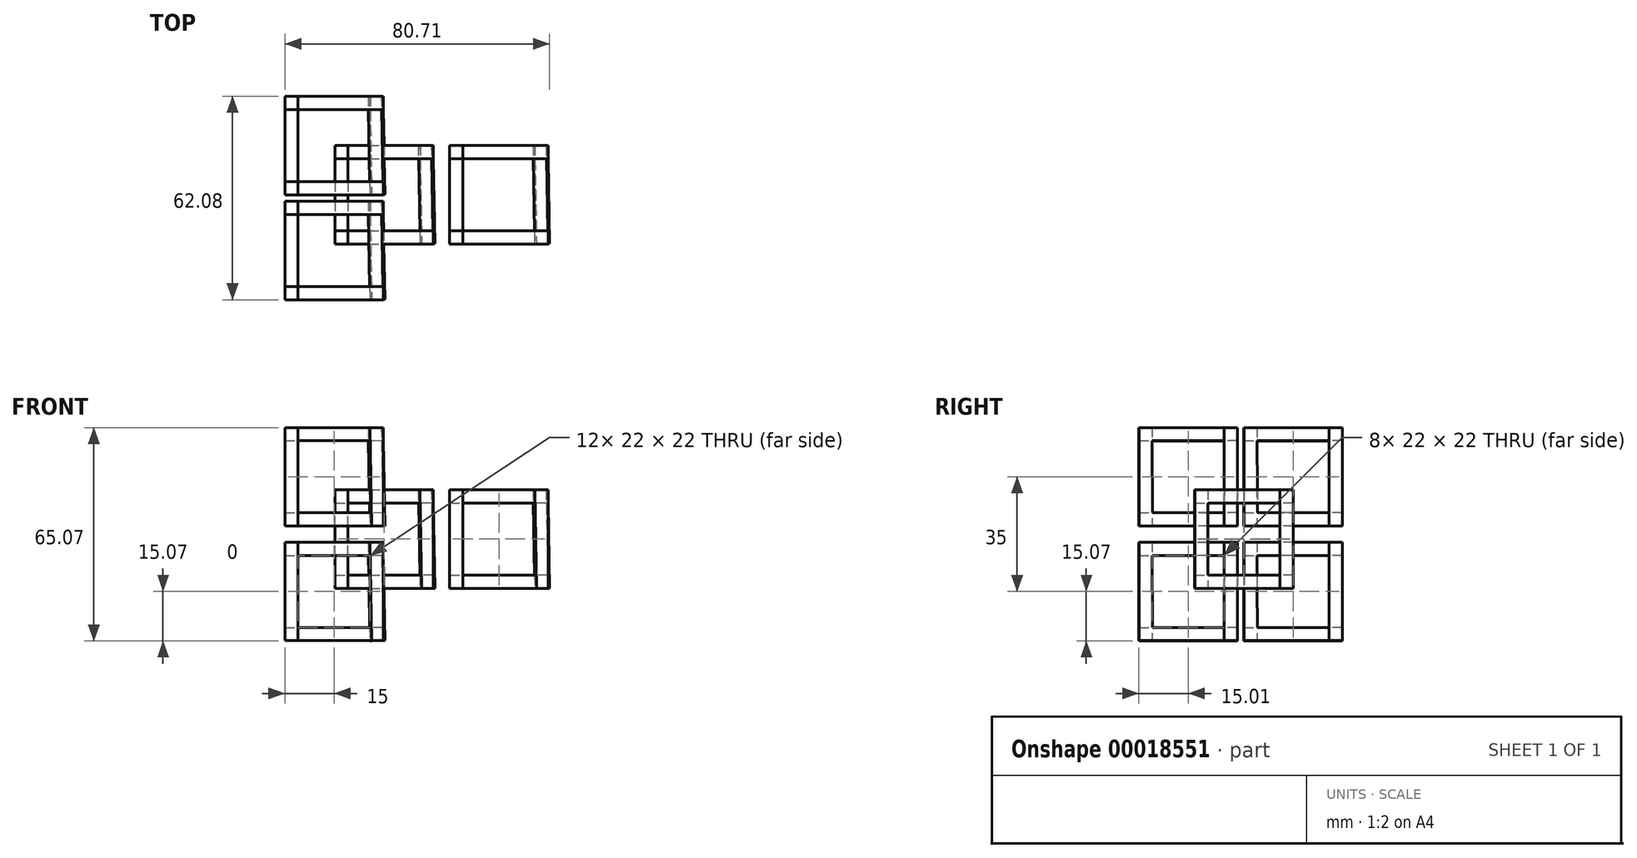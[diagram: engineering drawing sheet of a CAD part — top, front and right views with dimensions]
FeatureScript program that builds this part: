
annotation { "Feature Type Name" : "Feature", "Feature Type Description" : "" }
export const myFeature = defineFeature(function(context is Context, id is Id, definition is map)
    precondition{}
    {
        {
            var Q0;
            Q0=qCreatedBy(makeId("Top.planeOp"),FACE);
            var sketch = newSketch(context, id + "F0", { "sketchPlane" : qUnion([Q0])});
            skLineSegment(sketch, "E0.rect.bottom", {"start": v(-15, 15) * mm, "end": v(15, 15) * mm});
            skLineSegment(sketch, "E0.rect.top", {"start": v(-15, -15) * mm, "end": v(15, -15) * mm});
            skLineSegment(sketch, "E0.rect.left", {"start": v(-15, 15) * mm, "end": v(-15, -15) * mm});
            skLineSegment(sketch, "E0.rect.right", {"start": v(15, 15) * mm, "end": v(15, -15) * mm});
            skPoint(sketch, "E0.rect.middle", {"position": v(0, 0) * mm});
            skLineSegment(sketch, "E1.rect.bottom", {"start": v(-11, 11) * mm, "end": v(11, 11) * mm});
            skLineSegment(sketch, "E1.rect.top", {"start": v(-11, -11) * mm, "end": v(11, -11) * mm});
            skLineSegment(sketch, "E1.rect.left", {"start": v(-11, 11) * mm, "end": v(-11, -11) * mm});
            skLineSegment(sketch, "E1.rect.right", {"start": v(11, 11) * mm, "end": v(11, -11) * mm});
            skSolve(sketch);
        }
        {
            var Q0;
            Q0 = qSketchRegion(id + "F0", true);
            extrude(context, id + "F1", {"entities" : qUnion([Q0]), "depth" : 4 * mm});
        }
        {
            var Q0;
            Q0=makeQuery(id+"F1.opExtrude","SWEPT_BODY",BODY,{"disambiguationData":[OSD([sQuery(id+"F0.wireOp",EDGE,"E0.rect.bottom"),sQuery(id+"F0.wireOp",EDGE,"E0.rect.top"),sQuery(id+"F0.wireOp",EDGE,"E0.rect.left"),sQuery(id+"F0.wireOp",EDGE,"E0.rect.right"),sQuery(id+"F0.wireOp",EDGE,"E1.rect.bottom"),sQuery(id+"F0.wireOp",EDGE,"E1.rect.top"),sQuery(id+"F0.wireOp",EDGE,"E1.rect.left"),sQuery(id+"F0.wireOp",EDGE,"E1.rect.right")])]});
            var Q1;
            Q1=makeQuery(id+"F1.opExtrude","CAP_EDGE",EDGE,{"disambiguationData":[OSD([sQuery(id+"F0.wireOp",EDGE,"E0.rect.top")])],"isStart":false});
            transform(context, id + "F2", {"entities" : qUnion([Q0]), "transformType" : TransformType.ROTATION, "transformAxis" : qUnion([Q1]), "angle" : 90 * degree, "makeCopy" : true});
        }
        {
            var Q0;
            Q0=makeQuery(id+"F1.opExtrude","SWEPT_BODY",BODY,{"disambiguationData":[OSD([sQuery(id+"F0.wireOp",EDGE,"E0.rect.bottom"),sQuery(id+"F0.wireOp",EDGE,"E0.rect.top"),sQuery(id+"F0.wireOp",EDGE,"E0.rect.left"),sQuery(id+"F0.wireOp",EDGE,"E0.rect.right"),sQuery(id+"F0.wireOp",EDGE,"E1.rect.bottom"),sQuery(id+"F0.wireOp",EDGE,"E1.rect.top"),sQuery(id+"F0.wireOp",EDGE,"E1.rect.left"),sQuery(id+"F0.wireOp",EDGE,"E1.rect.right")])]});
            var Q1;
            Q1=makeQuery(id+"F1.opExtrude","CAP_EDGE",EDGE,{"disambiguationData":[OSD([sQuery(id+"F0.wireOp",EDGE,"E0.rect.bottom")])],"isStart":false});
            transform(context, id + "F3", {"entities" : qUnion([Q0]), "transformType" : TransformType.ROTATION, "transformAxis" : qUnion([Q1]), "angle" : 90 * degree, "oppositeDirection" : true, "makeCopy" : true});
        }
        {
            var Q0;
            Q0=makeQuery(id+"F1.opExtrude","SWEPT_BODY",BODY,{"disambiguationData":[OSD([sQuery(id+"F0.wireOp",EDGE,"E0.rect.bottom"),sQuery(id+"F0.wireOp",EDGE,"E0.rect.top"),sQuery(id+"F0.wireOp",EDGE,"E0.rect.left"),sQuery(id+"F0.wireOp",EDGE,"E0.rect.right"),sQuery(id+"F0.wireOp",EDGE,"E1.rect.bottom"),sQuery(id+"F0.wireOp",EDGE,"E1.rect.top"),sQuery(id+"F0.wireOp",EDGE,"E1.rect.left"),sQuery(id+"F0.wireOp",EDGE,"E1.rect.right")])]});
            var Q1;
            Q1=makeQuery(id+"F1.opExtrude","CAP_EDGE",EDGE,{"disambiguationData":[OSD([sQuery(id+"F0.wireOp",EDGE,"E0.rect.right")])],"isStart":false});
            transform(context, id + "F4", {"entities" : qUnion([Q0]), "transformType" : TransformType.ROTATION, "transformAxis" : qUnion([Q1]), "angle" : 89 * degree, "oppositeDirection" : true, "makeCopy" : true});
        }
        {
            var Q0;
            Q0=makeQuery(id+"F1.opExtrude","SWEPT_BODY",BODY,{"disambiguationData":[OSD([sQuery(id+"F0.wireOp",EDGE,"E0.rect.bottom"),sQuery(id+"F0.wireOp",EDGE,"E0.rect.top"),sQuery(id+"F0.wireOp",EDGE,"E0.rect.left"),sQuery(id+"F0.wireOp",EDGE,"E0.rect.right"),sQuery(id+"F0.wireOp",EDGE,"E1.rect.bottom"),sQuery(id+"F0.wireOp",EDGE,"E1.rect.top"),sQuery(id+"F0.wireOp",EDGE,"E1.rect.left"),sQuery(id+"F0.wireOp",EDGE,"E1.rect.right")])]});
            var Q1;
            Q1=makeQuery(id+"F1.opExtrude","CAP_EDGE",EDGE,{"disambiguationData":[OSD([sQuery(id+"F0.wireOp",EDGE,"E0.rect.left")])],"isStart":false});
            transform(context, id + "F5", {"entities" : qUnion([Q0]), "transformType" : TransformType.ROTATION, "transformAxis" : qUnion([Q1]), "angle" : 90 * degree, "makeCopy" : true});
        }
        {
            var Q0;
            Q0=makeQuery(id+"F1.opExtrude","SWEPT_BODY",BODY,{"disambiguationData":[OSD([sQuery(id+"F0.wireOp",EDGE,"E0.rect.bottom"),sQuery(id+"F0.wireOp",EDGE,"E0.rect.top"),sQuery(id+"F0.wireOp",EDGE,"E0.rect.left"),sQuery(id+"F0.wireOp",EDGE,"E0.rect.right"),sQuery(id+"F0.wireOp",EDGE,"E1.rect.bottom"),sQuery(id+"F0.wireOp",EDGE,"E1.rect.top"),sQuery(id+"F0.wireOp",EDGE,"E1.rect.left"),sQuery(id+"F0.wireOp",EDGE,"E1.rect.right")])]});
            deleteBodies(context, id + "F6", {"entities" : qUnion([Q0])});
        }
        {
            var Q0;
            Q0=makeQuery(id+"F4.opPattern","COPY",BODY,{"derivedFrom":makeQuery(id+"F1.opExtrude","SWEPT_BODY",BODY,{"disambiguationData":[OSD([sQuery(id+"F0.wireOp",EDGE,"E0.rect.bottom"),sQuery(id+"F0.wireOp",EDGE,"E0.rect.top"),sQuery(id+"F0.wireOp",EDGE,"E0.rect.left"),sQuery(id+"F0.wireOp",EDGE,"E0.rect.right"),sQuery(id+"F0.wireOp",EDGE,"E1.rect.bottom"),sQuery(id+"F0.wireOp",EDGE,"E1.rect.top"),sQuery(id+"F0.wireOp",EDGE,"E1.rect.left"),sQuery(id+"F0.wireOp",EDGE,"E1.rect.right")])]}),"instanceName":"1"});
            var Q1;
            Q1=makeQuery(id+"F3.opPattern","COPY",EDGE,{"derivedFrom":makeQuery(id+"F1.opExtrude","CAP_EDGE",EDGE,{"disambiguationData":[OSD([sQuery(id+"F0.wireOp",EDGE,"E1.rect.right")])],"isStart":true}),"instanceName":"1"});
            transform(context, id + "F7", {"entities" : qUnion([Q0]), "transformType" : TransformType.ROTATION, "transformAxis" : qUnion([Q1]), "angle" : 1 * degree, "makeCopy" : false});
        }
        {
            var Q0;
            Q0=makeQuery(id+"F2.opPattern","COPY",BODY,{"derivedFrom":makeQuery(id+"F1.opExtrude","SWEPT_BODY",BODY,{"disambiguationData":[OSD([sQuery(id+"F0.wireOp",EDGE,"E0.rect.bottom"),sQuery(id+"F0.wireOp",EDGE,"E0.rect.top"),sQuery(id+"F0.wireOp",EDGE,"E0.rect.left"),sQuery(id+"F0.wireOp",EDGE,"E0.rect.right"),sQuery(id+"F0.wireOp",EDGE,"E1.rect.bottom"),sQuery(id+"F0.wireOp",EDGE,"E1.rect.top"),sQuery(id+"F0.wireOp",EDGE,"E1.rect.left"),sQuery(id+"F0.wireOp",EDGE,"E1.rect.right")])]}),"instanceName":"1"});
            var Q1;
            Q1=makeQuery(id+"F3.opPattern","COPY",BODY,{"derivedFrom":makeQuery(id+"F1.opExtrude","SWEPT_BODY",BODY,{"disambiguationData":[OSD([sQuery(id+"F0.wireOp",EDGE,"E0.rect.bottom"),sQuery(id+"F0.wireOp",EDGE,"E0.rect.top"),sQuery(id+"F0.wireOp",EDGE,"E0.rect.left"),sQuery(id+"F0.wireOp",EDGE,"E0.rect.right"),sQuery(id+"F0.wireOp",EDGE,"E1.rect.bottom"),sQuery(id+"F0.wireOp",EDGE,"E1.rect.top"),sQuery(id+"F0.wireOp",EDGE,"E1.rect.left"),sQuery(id+"F0.wireOp",EDGE,"E1.rect.right")])]}),"instanceName":"1"});
            var Q2;
            Q2=makeQuery(id+"F4.opPattern","COPY",BODY,{"derivedFrom":makeQuery(id+"F1.opExtrude","SWEPT_BODY",BODY,{"disambiguationData":[OSD([sQuery(id+"F0.wireOp",EDGE,"E0.rect.bottom"),sQuery(id+"F0.wireOp",EDGE,"E0.rect.top"),sQuery(id+"F0.wireOp",EDGE,"E0.rect.left"),sQuery(id+"F0.wireOp",EDGE,"E0.rect.right"),sQuery(id+"F0.wireOp",EDGE,"E1.rect.bottom"),sQuery(id+"F0.wireOp",EDGE,"E1.rect.top"),sQuery(id+"F0.wireOp",EDGE,"E1.rect.left"),sQuery(id+"F0.wireOp",EDGE,"E1.rect.right")])]}),"instanceName":"1"});
            var Q3;
            Q3=makeQuery(id+"F5.opPattern","COPY",BODY,{"derivedFrom":makeQuery(id+"F1.opExtrude","SWEPT_BODY",BODY,{"disambiguationData":[OSD([sQuery(id+"F0.wireOp",EDGE,"E0.rect.bottom"),sQuery(id+"F0.wireOp",EDGE,"E0.rect.top"),sQuery(id+"F0.wireOp",EDGE,"E0.rect.left"),sQuery(id+"F0.wireOp",EDGE,"E0.rect.right"),sQuery(id+"F0.wireOp",EDGE,"E1.rect.bottom"),sQuery(id+"F0.wireOp",EDGE,"E1.rect.top"),sQuery(id+"F0.wireOp",EDGE,"E1.rect.left"),sQuery(id+"F0.wireOp",EDGE,"E1.rect.right")])]}),"instanceName":"1"});
            var Q4;
            Q4=makeQuery(id+"F5.opPattern","COPY",EDGE,{"derivedFrom":makeQuery(id+"F1.opExtrude","CAP_EDGE",EDGE,{"disambiguationData":[OSD([sQuery(id+"F0.wireOp",EDGE,"E0.rect.right")])],"isStart":false}),"instanceName":"1"});
            transform(context, id + "F8", {"entities" : qUnion([Q0, Q1, Q2, Q3]), "transformType" : TransformType.TRANSLATION_DISTANCE, "transformDirection" : qUnion([Q4]), "distance" : 32 * mm, "oppositeDirection" : true, "makeCopy" : true});
        }
        {
            var Q0;
            Q0=makeQuery(id+"F8.opPattern","COPY",BODY,{"derivedFrom":makeQuery(id+"F5.opPattern","COPY",BODY,{"derivedFrom":makeQuery(id+"F1.opExtrude","SWEPT_BODY",BODY,{"disambiguationData":[OSD([sQuery(id+"F0.wireOp",EDGE,"E0.rect.bottom"),sQuery(id+"F0.wireOp",EDGE,"E0.rect.top"),sQuery(id+"F0.wireOp",EDGE,"E0.rect.left"),sQuery(id+"F0.wireOp",EDGE,"E0.rect.right"),sQuery(id+"F0.wireOp",EDGE,"E1.rect.bottom"),sQuery(id+"F0.wireOp",EDGE,"E1.rect.top"),sQuery(id+"F0.wireOp",EDGE,"E1.rect.left"),sQuery(id+"F0.wireOp",EDGE,"E1.rect.right")])]}),"instanceName":"1"}),"instanceName":"1"});
            var Q1;
            Q1=makeQuery(id+"F8.opPattern","COPY",BODY,{"derivedFrom":makeQuery(id+"F4.opPattern","COPY",BODY,{"derivedFrom":makeQuery(id+"F1.opExtrude","SWEPT_BODY",BODY,{"disambiguationData":[OSD([sQuery(id+"F0.wireOp",EDGE,"E0.rect.bottom"),sQuery(id+"F0.wireOp",EDGE,"E0.rect.top"),sQuery(id+"F0.wireOp",EDGE,"E0.rect.left"),sQuery(id+"F0.wireOp",EDGE,"E0.rect.right"),sQuery(id+"F0.wireOp",EDGE,"E1.rect.bottom"),sQuery(id+"F0.wireOp",EDGE,"E1.rect.top"),sQuery(id+"F0.wireOp",EDGE,"E1.rect.left"),sQuery(id+"F0.wireOp",EDGE,"E1.rect.right")])]}),"instanceName":"1"}),"instanceName":"1"});
            var Q2;
            Q2=makeQuery(id+"F8.opPattern","COPY",BODY,{"derivedFrom":makeQuery(id+"F3.opPattern","COPY",BODY,{"derivedFrom":makeQuery(id+"F1.opExtrude","SWEPT_BODY",BODY,{"disambiguationData":[OSD([sQuery(id+"F0.wireOp",EDGE,"E0.rect.bottom"),sQuery(id+"F0.wireOp",EDGE,"E0.rect.top"),sQuery(id+"F0.wireOp",EDGE,"E0.rect.left"),sQuery(id+"F0.wireOp",EDGE,"E0.rect.right"),sQuery(id+"F0.wireOp",EDGE,"E1.rect.bottom"),sQuery(id+"F0.wireOp",EDGE,"E1.rect.top"),sQuery(id+"F0.wireOp",EDGE,"E1.rect.left"),sQuery(id+"F0.wireOp",EDGE,"E1.rect.right")])]}),"instanceName":"1"}),"instanceName":"1"});
            var Q3;
            Q3=makeQuery(id+"F8.opPattern","COPY",BODY,{"derivedFrom":makeQuery(id+"F2.opPattern","COPY",BODY,{"derivedFrom":makeQuery(id+"F1.opExtrude","SWEPT_BODY",BODY,{"disambiguationData":[OSD([sQuery(id+"F0.wireOp",EDGE,"E0.rect.bottom"),sQuery(id+"F0.wireOp",EDGE,"E0.rect.top"),sQuery(id+"F0.wireOp",EDGE,"E0.rect.left"),sQuery(id+"F0.wireOp",EDGE,"E0.rect.right"),sQuery(id+"F0.wireOp",EDGE,"E1.rect.bottom"),sQuery(id+"F0.wireOp",EDGE,"E1.rect.top"),sQuery(id+"F0.wireOp",EDGE,"E1.rect.left"),sQuery(id+"F0.wireOp",EDGE,"E1.rect.right")])]}),"instanceName":"1"}),"instanceName":"1"});
            var Q4;
            Q4=makeQuery(id+"F8.opPattern","COPY",EDGE,{"derivedFrom":makeQuery(id+"F4.opPattern","COPY",EDGE,{"derivedFrom":makeQuery(id+"F1.opExtrude","CAP_EDGE",EDGE,{"disambiguationData":[OSD([sQuery(id+"F0.wireOp",EDGE,"E1.rect.right")])],"isStart":true}),"instanceName":"1"}),"instanceName":"1"});
            transform(context, id + "F9", {"entities" : qUnion([Q0, Q1, Q2, Q3]), "transformType" : TransformType.TRANSLATION_DISTANCE, "transformDirection" : qUnion([Q4]), "distance" : 15 * mm, "makeCopy" : true});
        }
        {
            var Q0;
            Q0=makeQuery(id+"F9.opPattern","COPY",BODY,{"derivedFrom":makeQuery(id+"F8.opPattern","COPY",BODY,{"derivedFrom":makeQuery(id+"F5.opPattern","COPY",BODY,{"derivedFrom":makeQuery(id+"F1.opExtrude","SWEPT_BODY",BODY,{"disambiguationData":[OSD([sQuery(id+"F0.wireOp",EDGE,"E0.rect.bottom"),sQuery(id+"F0.wireOp",EDGE,"E0.rect.top"),sQuery(id+"F0.wireOp",EDGE,"E0.rect.left"),sQuery(id+"F0.wireOp",EDGE,"E0.rect.right"),sQuery(id+"F0.wireOp",EDGE,"E1.rect.bottom"),sQuery(id+"F0.wireOp",EDGE,"E1.rect.top"),sQuery(id+"F0.wireOp",EDGE,"E1.rect.left"),sQuery(id+"F0.wireOp",EDGE,"E1.rect.right")])]}),"instanceName":"1"}),"instanceName":"1"}),"instanceName":"1"});
            var Q1;
            Q1=makeQuery(id+"F9.opPattern","COPY",BODY,{"derivedFrom":makeQuery(id+"F8.opPattern","COPY",BODY,{"derivedFrom":makeQuery(id+"F4.opPattern","COPY",BODY,{"derivedFrom":makeQuery(id+"F1.opExtrude","SWEPT_BODY",BODY,{"disambiguationData":[OSD([sQuery(id+"F0.wireOp",EDGE,"E0.rect.bottom"),sQuery(id+"F0.wireOp",EDGE,"E0.rect.top"),sQuery(id+"F0.wireOp",EDGE,"E0.rect.left"),sQuery(id+"F0.wireOp",EDGE,"E0.rect.right"),sQuery(id+"F0.wireOp",EDGE,"E1.rect.bottom"),sQuery(id+"F0.wireOp",EDGE,"E1.rect.top"),sQuery(id+"F0.wireOp",EDGE,"E1.rect.left"),sQuery(id+"F0.wireOp",EDGE,"E1.rect.right")])]}),"instanceName":"1"}),"instanceName":"1"}),"instanceName":"1"});
            var Q2;
            Q2=makeQuery(id+"F9.opPattern","COPY",BODY,{"derivedFrom":makeQuery(id+"F8.opPattern","COPY",BODY,{"derivedFrom":makeQuery(id+"F3.opPattern","COPY",BODY,{"derivedFrom":makeQuery(id+"F1.opExtrude","SWEPT_BODY",BODY,{"disambiguationData":[OSD([sQuery(id+"F0.wireOp",EDGE,"E0.rect.bottom"),sQuery(id+"F0.wireOp",EDGE,"E0.rect.top"),sQuery(id+"F0.wireOp",EDGE,"E0.rect.left"),sQuery(id+"F0.wireOp",EDGE,"E0.rect.right"),sQuery(id+"F0.wireOp",EDGE,"E1.rect.bottom"),sQuery(id+"F0.wireOp",EDGE,"E1.rect.top"),sQuery(id+"F0.wireOp",EDGE,"E1.rect.left"),sQuery(id+"F0.wireOp",EDGE,"E1.rect.right")])]}),"instanceName":"1"}),"instanceName":"1"}),"instanceName":"1"});
            var Q3;
            Q3=makeQuery(id+"F9.opPattern","COPY",BODY,{"derivedFrom":makeQuery(id+"F8.opPattern","COPY",BODY,{"derivedFrom":makeQuery(id+"F2.opPattern","COPY",BODY,{"derivedFrom":makeQuery(id+"F1.opExtrude","SWEPT_BODY",BODY,{"disambiguationData":[OSD([sQuery(id+"F0.wireOp",EDGE,"E0.rect.bottom"),sQuery(id+"F0.wireOp",EDGE,"E0.rect.top"),sQuery(id+"F0.wireOp",EDGE,"E0.rect.left"),sQuery(id+"F0.wireOp",EDGE,"E0.rect.right"),sQuery(id+"F0.wireOp",EDGE,"E1.rect.bottom"),sQuery(id+"F0.wireOp",EDGE,"E1.rect.top"),sQuery(id+"F0.wireOp",EDGE,"E1.rect.left"),sQuery(id+"F0.wireOp",EDGE,"E1.rect.right")])]}),"instanceName":"1"}),"instanceName":"1"}),"instanceName":"1"});
            var Q4;
            Q4=makeQuery(id+"F9.opPattern","COPY",EDGE,{"derivedFrom":makeQuery(id+"F8.opPattern","COPY",EDGE,{"derivedFrom":makeQuery(id+"F3.opPattern","COPY",EDGE,{"derivedFrom":makeQuery(id+"F1.opExtrude","CAP_EDGE",EDGE,{"disambiguationData":[OSD([sQuery(id+"F0.wireOp",EDGE,"E0.rect.bottom")])],"isStart":true}),"instanceName":"1"}),"instanceName":"1"}),"instanceName":"1"});
            transform(context, id + "F10", {"entities" : qUnion([Q0, Q1, Q2, Q3]), "transformType" : TransformType.TRANSLATION_DISTANCE, "transformDirection" : qUnion([Q4]), "distance" : 15 * mm, "makeCopy" : false});
        }
        {
            var Q0;
            Q0=makeQuery(id+"F9.opPattern","COPY",BODY,{"derivedFrom":makeQuery(id+"F8.opPattern","COPY",BODY,{"derivedFrom":makeQuery(id+"F5.opPattern","COPY",BODY,{"derivedFrom":makeQuery(id+"F1.opExtrude","SWEPT_BODY",BODY,{"disambiguationData":[OSD([sQuery(id+"F0.wireOp",EDGE,"E0.rect.bottom"),sQuery(id+"F0.wireOp",EDGE,"E0.rect.top"),sQuery(id+"F0.wireOp",EDGE,"E0.rect.left"),sQuery(id+"F0.wireOp",EDGE,"E0.rect.right"),sQuery(id+"F0.wireOp",EDGE,"E1.rect.bottom"),sQuery(id+"F0.wireOp",EDGE,"E1.rect.top"),sQuery(id+"F0.wireOp",EDGE,"E1.rect.left"),sQuery(id+"F0.wireOp",EDGE,"E1.rect.right")])]}),"instanceName":"1"}),"instanceName":"1"}),"instanceName":"1"});
            var Q1;
            Q1=makeQuery(id+"F9.opPattern","COPY",BODY,{"derivedFrom":makeQuery(id+"F8.opPattern","COPY",BODY,{"derivedFrom":makeQuery(id+"F4.opPattern","COPY",BODY,{"derivedFrom":makeQuery(id+"F1.opExtrude","SWEPT_BODY",BODY,{"disambiguationData":[OSD([sQuery(id+"F0.wireOp",EDGE,"E0.rect.bottom"),sQuery(id+"F0.wireOp",EDGE,"E0.rect.top"),sQuery(id+"F0.wireOp",EDGE,"E0.rect.left"),sQuery(id+"F0.wireOp",EDGE,"E0.rect.right"),sQuery(id+"F0.wireOp",EDGE,"E1.rect.bottom"),sQuery(id+"F0.wireOp",EDGE,"E1.rect.top"),sQuery(id+"F0.wireOp",EDGE,"E1.rect.left"),sQuery(id+"F0.wireOp",EDGE,"E1.rect.right")])]}),"instanceName":"1"}),"instanceName":"1"}),"instanceName":"1"});
            var Q2;
            Q2=makeQuery(id+"F9.opPattern","COPY",BODY,{"derivedFrom":makeQuery(id+"F8.opPattern","COPY",BODY,{"derivedFrom":makeQuery(id+"F3.opPattern","COPY",BODY,{"derivedFrom":makeQuery(id+"F1.opExtrude","SWEPT_BODY",BODY,{"disambiguationData":[OSD([sQuery(id+"F0.wireOp",EDGE,"E0.rect.bottom"),sQuery(id+"F0.wireOp",EDGE,"E0.rect.top"),sQuery(id+"F0.wireOp",EDGE,"E0.rect.left"),sQuery(id+"F0.wireOp",EDGE,"E0.rect.right"),sQuery(id+"F0.wireOp",EDGE,"E1.rect.bottom"),sQuery(id+"F0.wireOp",EDGE,"E1.rect.top"),sQuery(id+"F0.wireOp",EDGE,"E1.rect.left"),sQuery(id+"F0.wireOp",EDGE,"E1.rect.right")])]}),"instanceName":"1"}),"instanceName":"1"}),"instanceName":"1"});
            var Q3;
            Q3=makeQuery(id+"F9.opPattern","COPY",BODY,{"derivedFrom":makeQuery(id+"F8.opPattern","COPY",BODY,{"derivedFrom":makeQuery(id+"F2.opPattern","COPY",BODY,{"derivedFrom":makeQuery(id+"F1.opExtrude","SWEPT_BODY",BODY,{"disambiguationData":[OSD([sQuery(id+"F0.wireOp",EDGE,"E0.rect.bottom"),sQuery(id+"F0.wireOp",EDGE,"E0.rect.top"),sQuery(id+"F0.wireOp",EDGE,"E0.rect.left"),sQuery(id+"F0.wireOp",EDGE,"E0.rect.right"),sQuery(id+"F0.wireOp",EDGE,"E1.rect.bottom"),sQuery(id+"F0.wireOp",EDGE,"E1.rect.top"),sQuery(id+"F0.wireOp",EDGE,"E1.rect.left"),sQuery(id+"F0.wireOp",EDGE,"E1.rect.right")])]}),"instanceName":"1"}),"instanceName":"1"}),"instanceName":"1"});
            var Q4;
            Q4=qCreatedBy(makeId("Top.planeOp"),FACE);
            transform(context, id + "F11", {"entities" : qUnion([Q0, Q1, Q2, Q3]), "transformType" : TransformType.TRANSLATION_DISTANCE, "transformDirection" : qUnion([Q4]), "distance" : 15 * mm, "oppositeDirection" : true, "makeCopy" : false});
        }
        {
            var Q0;
            Q0=makeQuery(id+"F2.opPattern","COPY",BODY,{"derivedFrom":makeQuery(id+"F1.opExtrude","SWEPT_BODY",BODY,{"disambiguationData":[OSD([sQuery(id+"F0.wireOp",EDGE,"E0.rect.bottom"),sQuery(id+"F0.wireOp",EDGE,"E0.rect.top"),sQuery(id+"F0.wireOp",EDGE,"E0.rect.left"),sQuery(id+"F0.wireOp",EDGE,"E0.rect.right"),sQuery(id+"F0.wireOp",EDGE,"E1.rect.bottom"),sQuery(id+"F0.wireOp",EDGE,"E1.rect.top"),sQuery(id+"F0.wireOp",EDGE,"E1.rect.left"),sQuery(id+"F0.wireOp",EDGE,"E1.rect.right")])]}),"instanceName":"1"});
            var Q1;
            Q1=makeQuery(id+"F3.opPattern","COPY",BODY,{"derivedFrom":makeQuery(id+"F1.opExtrude","SWEPT_BODY",BODY,{"disambiguationData":[OSD([sQuery(id+"F0.wireOp",EDGE,"E0.rect.bottom"),sQuery(id+"F0.wireOp",EDGE,"E0.rect.top"),sQuery(id+"F0.wireOp",EDGE,"E0.rect.left"),sQuery(id+"F0.wireOp",EDGE,"E0.rect.right"),sQuery(id+"F0.wireOp",EDGE,"E1.rect.bottom"),sQuery(id+"F0.wireOp",EDGE,"E1.rect.top"),sQuery(id+"F0.wireOp",EDGE,"E1.rect.left"),sQuery(id+"F0.wireOp",EDGE,"E1.rect.right")])]}),"instanceName":"1"});
            var Q2;
            Q2=makeQuery(id+"F4.opPattern","COPY",BODY,{"derivedFrom":makeQuery(id+"F1.opExtrude","SWEPT_BODY",BODY,{"disambiguationData":[OSD([sQuery(id+"F0.wireOp",EDGE,"E0.rect.bottom"),sQuery(id+"F0.wireOp",EDGE,"E0.rect.top"),sQuery(id+"F0.wireOp",EDGE,"E0.rect.left"),sQuery(id+"F0.wireOp",EDGE,"E0.rect.right"),sQuery(id+"F0.wireOp",EDGE,"E1.rect.bottom"),sQuery(id+"F0.wireOp",EDGE,"E1.rect.top"),sQuery(id+"F0.wireOp",EDGE,"E1.rect.left"),sQuery(id+"F0.wireOp",EDGE,"E1.rect.right")])]}),"instanceName":"1"});
            var Q3;
            Q3=makeQuery(id+"F5.opPattern","COPY",BODY,{"derivedFrom":makeQuery(id+"F1.opExtrude","SWEPT_BODY",BODY,{"disambiguationData":[OSD([sQuery(id+"F0.wireOp",EDGE,"E0.rect.bottom"),sQuery(id+"F0.wireOp",EDGE,"E0.rect.top"),sQuery(id+"F0.wireOp",EDGE,"E0.rect.left"),sQuery(id+"F0.wireOp",EDGE,"E0.rect.right"),sQuery(id+"F0.wireOp",EDGE,"E1.rect.bottom"),sQuery(id+"F0.wireOp",EDGE,"E1.rect.top"),sQuery(id+"F0.wireOp",EDGE,"E1.rect.left"),sQuery(id+"F0.wireOp",EDGE,"E1.rect.right")])]}),"instanceName":"1"});
            var Q4;
            Q4=makeQuery(id+"F8.opPattern","COPY",BODY,{"derivedFrom":makeQuery(id+"F2.opPattern","COPY",BODY,{"derivedFrom":makeQuery(id+"F1.opExtrude","SWEPT_BODY",BODY,{"disambiguationData":[OSD([sQuery(id+"F0.wireOp",EDGE,"E0.rect.bottom"),sQuery(id+"F0.wireOp",EDGE,"E0.rect.top"),sQuery(id+"F0.wireOp",EDGE,"E0.rect.left"),sQuery(id+"F0.wireOp",EDGE,"E0.rect.right"),sQuery(id+"F0.wireOp",EDGE,"E1.rect.bottom"),sQuery(id+"F0.wireOp",EDGE,"E1.rect.top"),sQuery(id+"F0.wireOp",EDGE,"E1.rect.left"),sQuery(id+"F0.wireOp",EDGE,"E1.rect.right")])]}),"instanceName":"1"}),"instanceName":"1"});
            var Q5;
            Q5=makeQuery(id+"F8.opPattern","COPY",BODY,{"derivedFrom":makeQuery(id+"F3.opPattern","COPY",BODY,{"derivedFrom":makeQuery(id+"F1.opExtrude","SWEPT_BODY",BODY,{"disambiguationData":[OSD([sQuery(id+"F0.wireOp",EDGE,"E0.rect.bottom"),sQuery(id+"F0.wireOp",EDGE,"E0.rect.top"),sQuery(id+"F0.wireOp",EDGE,"E0.rect.left"),sQuery(id+"F0.wireOp",EDGE,"E0.rect.right"),sQuery(id+"F0.wireOp",EDGE,"E1.rect.bottom"),sQuery(id+"F0.wireOp",EDGE,"E1.rect.top"),sQuery(id+"F0.wireOp",EDGE,"E1.rect.left"),sQuery(id+"F0.wireOp",EDGE,"E1.rect.right")])]}),"instanceName":"1"}),"instanceName":"1"});
            var Q6;
            Q6=makeQuery(id+"F8.opPattern","COPY",BODY,{"derivedFrom":makeQuery(id+"F4.opPattern","COPY",BODY,{"derivedFrom":makeQuery(id+"F1.opExtrude","SWEPT_BODY",BODY,{"disambiguationData":[OSD([sQuery(id+"F0.wireOp",EDGE,"E0.rect.bottom"),sQuery(id+"F0.wireOp",EDGE,"E0.rect.top"),sQuery(id+"F0.wireOp",EDGE,"E0.rect.left"),sQuery(id+"F0.wireOp",EDGE,"E0.rect.right"),sQuery(id+"F0.wireOp",EDGE,"E1.rect.bottom"),sQuery(id+"F0.wireOp",EDGE,"E1.rect.top"),sQuery(id+"F0.wireOp",EDGE,"E1.rect.left"),sQuery(id+"F0.wireOp",EDGE,"E1.rect.right")])]}),"instanceName":"1"}),"instanceName":"1"});
            var Q7;
            Q7=makeQuery(id+"F8.opPattern","COPY",BODY,{"derivedFrom":makeQuery(id+"F5.opPattern","COPY",BODY,{"derivedFrom":makeQuery(id+"F1.opExtrude","SWEPT_BODY",BODY,{"disambiguationData":[OSD([sQuery(id+"F0.wireOp",EDGE,"E0.rect.bottom"),sQuery(id+"F0.wireOp",EDGE,"E0.rect.top"),sQuery(id+"F0.wireOp",EDGE,"E0.rect.left"),sQuery(id+"F0.wireOp",EDGE,"E0.rect.right"),sQuery(id+"F0.wireOp",EDGE,"E1.rect.bottom"),sQuery(id+"F0.wireOp",EDGE,"E1.rect.top"),sQuery(id+"F0.wireOp",EDGE,"E1.rect.left"),sQuery(id+"F0.wireOp",EDGE,"E1.rect.right")])]}),"instanceName":"1"}),"instanceName":"1"});
            var Q8;
            Q8=qCreatedBy(makeId("Top.planeOp"),FACE);
            transform(context, id + "F12", {"entities" : qUnion([Q0, Q1, Q2, Q3, Q4, Q5, Q6, Q7]), "transformType" : TransformType.TRANSLATION_DISTANCE, "transformDirection" : qUnion([Q8]), "distance" : 4 * mm, "makeCopy" : false});
        }
        {
            var Q0;
            Q0=makeQuery(id+"F2.opPattern","COPY",BODY,{"derivedFrom":makeQuery(id+"F1.opExtrude","SWEPT_BODY",BODY,{"disambiguationData":[OSD([sQuery(id+"F0.wireOp",EDGE,"E0.rect.bottom"),sQuery(id+"F0.wireOp",EDGE,"E0.rect.top"),sQuery(id+"F0.wireOp",EDGE,"E0.rect.left"),sQuery(id+"F0.wireOp",EDGE,"E0.rect.right"),sQuery(id+"F0.wireOp",EDGE,"E1.rect.bottom"),sQuery(id+"F0.wireOp",EDGE,"E1.rect.top"),sQuery(id+"F0.wireOp",EDGE,"E1.rect.left"),sQuery(id+"F0.wireOp",EDGE,"E1.rect.right")])]}),"instanceName":"1"});
            var Q1;
            Q1=makeQuery(id+"F3.opPattern","COPY",BODY,{"derivedFrom":makeQuery(id+"F1.opExtrude","SWEPT_BODY",BODY,{"disambiguationData":[OSD([sQuery(id+"F0.wireOp",EDGE,"E0.rect.bottom"),sQuery(id+"F0.wireOp",EDGE,"E0.rect.top"),sQuery(id+"F0.wireOp",EDGE,"E0.rect.left"),sQuery(id+"F0.wireOp",EDGE,"E0.rect.right"),sQuery(id+"F0.wireOp",EDGE,"E1.rect.bottom"),sQuery(id+"F0.wireOp",EDGE,"E1.rect.top"),sQuery(id+"F0.wireOp",EDGE,"E1.rect.left"),sQuery(id+"F0.wireOp",EDGE,"E1.rect.right")])]}),"instanceName":"1"});
            var Q2;
            Q2=makeQuery(id+"F4.opPattern","COPY",BODY,{"derivedFrom":makeQuery(id+"F1.opExtrude","SWEPT_BODY",BODY,{"disambiguationData":[OSD([sQuery(id+"F0.wireOp",EDGE,"E0.rect.bottom"),sQuery(id+"F0.wireOp",EDGE,"E0.rect.top"),sQuery(id+"F0.wireOp",EDGE,"E0.rect.left"),sQuery(id+"F0.wireOp",EDGE,"E0.rect.right"),sQuery(id+"F0.wireOp",EDGE,"E1.rect.bottom"),sQuery(id+"F0.wireOp",EDGE,"E1.rect.top"),sQuery(id+"F0.wireOp",EDGE,"E1.rect.left"),sQuery(id+"F0.wireOp",EDGE,"E1.rect.right")])]}),"instanceName":"1"});
            var Q3;
            Q3=makeQuery(id+"F5.opPattern","COPY",BODY,{"derivedFrom":makeQuery(id+"F1.opExtrude","SWEPT_BODY",BODY,{"disambiguationData":[OSD([sQuery(id+"F0.wireOp",EDGE,"E0.rect.bottom"),sQuery(id+"F0.wireOp",EDGE,"E0.rect.top"),sQuery(id+"F0.wireOp",EDGE,"E0.rect.left"),sQuery(id+"F0.wireOp",EDGE,"E0.rect.right"),sQuery(id+"F0.wireOp",EDGE,"E1.rect.bottom"),sQuery(id+"F0.wireOp",EDGE,"E1.rect.top"),sQuery(id+"F0.wireOp",EDGE,"E1.rect.left"),sQuery(id+"F0.wireOp",EDGE,"E1.rect.right")])]}),"instanceName":"1"});
            var Q4;
            Q4=makeQuery(id+"F8.opPattern","COPY",BODY,{"derivedFrom":makeQuery(id+"F2.opPattern","COPY",BODY,{"derivedFrom":makeQuery(id+"F1.opExtrude","SWEPT_BODY",BODY,{"disambiguationData":[OSD([sQuery(id+"F0.wireOp",EDGE,"E0.rect.bottom"),sQuery(id+"F0.wireOp",EDGE,"E0.rect.top"),sQuery(id+"F0.wireOp",EDGE,"E0.rect.left"),sQuery(id+"F0.wireOp",EDGE,"E0.rect.right"),sQuery(id+"F0.wireOp",EDGE,"E1.rect.bottom"),sQuery(id+"F0.wireOp",EDGE,"E1.rect.top"),sQuery(id+"F0.wireOp",EDGE,"E1.rect.left"),sQuery(id+"F0.wireOp",EDGE,"E1.rect.right")])]}),"instanceName":"1"}),"instanceName":"1"});
            var Q5;
            Q5=makeQuery(id+"F8.opPattern","COPY",BODY,{"derivedFrom":makeQuery(id+"F3.opPattern","COPY",BODY,{"derivedFrom":makeQuery(id+"F1.opExtrude","SWEPT_BODY",BODY,{"disambiguationData":[OSD([sQuery(id+"F0.wireOp",EDGE,"E0.rect.bottom"),sQuery(id+"F0.wireOp",EDGE,"E0.rect.top"),sQuery(id+"F0.wireOp",EDGE,"E0.rect.left"),sQuery(id+"F0.wireOp",EDGE,"E0.rect.right"),sQuery(id+"F0.wireOp",EDGE,"E1.rect.bottom"),sQuery(id+"F0.wireOp",EDGE,"E1.rect.top"),sQuery(id+"F0.wireOp",EDGE,"E1.rect.left"),sQuery(id+"F0.wireOp",EDGE,"E1.rect.right")])]}),"instanceName":"1"}),"instanceName":"1"});
            var Q6;
            Q6=makeQuery(id+"F8.opPattern","COPY",BODY,{"derivedFrom":makeQuery(id+"F4.opPattern","COPY",BODY,{"derivedFrom":makeQuery(id+"F1.opExtrude","SWEPT_BODY",BODY,{"disambiguationData":[OSD([sQuery(id+"F0.wireOp",EDGE,"E0.rect.bottom"),sQuery(id+"F0.wireOp",EDGE,"E0.rect.top"),sQuery(id+"F0.wireOp",EDGE,"E0.rect.left"),sQuery(id+"F0.wireOp",EDGE,"E0.rect.right"),sQuery(id+"F0.wireOp",EDGE,"E1.rect.bottom"),sQuery(id+"F0.wireOp",EDGE,"E1.rect.top"),sQuery(id+"F0.wireOp",EDGE,"E1.rect.left"),sQuery(id+"F0.wireOp",EDGE,"E1.rect.right")])]}),"instanceName":"1"}),"instanceName":"1"});
            var Q7;
            Q7=makeQuery(id+"F8.opPattern","COPY",BODY,{"derivedFrom":makeQuery(id+"F5.opPattern","COPY",BODY,{"derivedFrom":makeQuery(id+"F1.opExtrude","SWEPT_BODY",BODY,{"disambiguationData":[OSD([sQuery(id+"F0.wireOp",EDGE,"E0.rect.bottom"),sQuery(id+"F0.wireOp",EDGE,"E0.rect.top"),sQuery(id+"F0.wireOp",EDGE,"E0.rect.left"),sQuery(id+"F0.wireOp",EDGE,"E0.rect.right"),sQuery(id+"F0.wireOp",EDGE,"E1.rect.bottom"),sQuery(id+"F0.wireOp",EDGE,"E1.rect.top"),sQuery(id+"F0.wireOp",EDGE,"E1.rect.left"),sQuery(id+"F0.wireOp",EDGE,"E1.rect.right")])]}),"instanceName":"1"}),"instanceName":"1"});
            var Q8;
            Q8=qCreatedBy(makeId("Top.planeOp"),FACE);
            transform(context, id + "F13", {"entities" : qUnion([Q0, Q1, Q2, Q3, Q4, Q5, Q6, Q7]), "transformType" : TransformType.TRANSLATION_DISTANCE, "transformDirection" : qUnion([Q8]), "distance" : 35 * mm, "oppositeDirection" : true, "makeCopy" : true});
        }
        {
            var Q0;
            Q0=makeQuery(id+"F9.opPattern","COPY",BODY,{"derivedFrom":makeQuery(id+"F8.opPattern","COPY",BODY,{"derivedFrom":makeQuery(id+"F2.opPattern","COPY",BODY,{"derivedFrom":makeQuery(id+"F1.opExtrude","SWEPT_BODY",BODY,{"disambiguationData":[OSD([sQuery(id+"F0.wireOp",EDGE,"E0.rect.bottom"),sQuery(id+"F0.wireOp",EDGE,"E0.rect.top"),sQuery(id+"F0.wireOp",EDGE,"E0.rect.left"),sQuery(id+"F0.wireOp",EDGE,"E0.rect.right"),sQuery(id+"F0.wireOp",EDGE,"E1.rect.bottom"),sQuery(id+"F0.wireOp",EDGE,"E1.rect.top"),sQuery(id+"F0.wireOp",EDGE,"E1.rect.left"),sQuery(id+"F0.wireOp",EDGE,"E1.rect.right")])]}),"instanceName":"1"}),"instanceName":"1"}),"instanceName":"1"});
            var Q1;
            Q1=makeQuery(id+"F9.opPattern","COPY",BODY,{"derivedFrom":makeQuery(id+"F8.opPattern","COPY",BODY,{"derivedFrom":makeQuery(id+"F3.opPattern","COPY",BODY,{"derivedFrom":makeQuery(id+"F1.opExtrude","SWEPT_BODY",BODY,{"disambiguationData":[OSD([sQuery(id+"F0.wireOp",EDGE,"E0.rect.bottom"),sQuery(id+"F0.wireOp",EDGE,"E0.rect.top"),sQuery(id+"F0.wireOp",EDGE,"E0.rect.left"),sQuery(id+"F0.wireOp",EDGE,"E0.rect.right"),sQuery(id+"F0.wireOp",EDGE,"E1.rect.bottom"),sQuery(id+"F0.wireOp",EDGE,"E1.rect.top"),sQuery(id+"F0.wireOp",EDGE,"E1.rect.left"),sQuery(id+"F0.wireOp",EDGE,"E1.rect.right")])]}),"instanceName":"1"}),"instanceName":"1"}),"instanceName":"1"});
            var Q2;
            Q2=makeQuery(id+"F9.opPattern","COPY",BODY,{"derivedFrom":makeQuery(id+"F8.opPattern","COPY",BODY,{"derivedFrom":makeQuery(id+"F4.opPattern","COPY",BODY,{"derivedFrom":makeQuery(id+"F1.opExtrude","SWEPT_BODY",BODY,{"disambiguationData":[OSD([sQuery(id+"F0.wireOp",EDGE,"E0.rect.bottom"),sQuery(id+"F0.wireOp",EDGE,"E0.rect.top"),sQuery(id+"F0.wireOp",EDGE,"E0.rect.left"),sQuery(id+"F0.wireOp",EDGE,"E0.rect.right"),sQuery(id+"F0.wireOp",EDGE,"E1.rect.bottom"),sQuery(id+"F0.wireOp",EDGE,"E1.rect.top"),sQuery(id+"F0.wireOp",EDGE,"E1.rect.left"),sQuery(id+"F0.wireOp",EDGE,"E1.rect.right")])]}),"instanceName":"1"}),"instanceName":"1"}),"instanceName":"1"});
            var Q3;
            Q3=makeQuery(id+"F9.opPattern","COPY",BODY,{"derivedFrom":makeQuery(id+"F8.opPattern","COPY",BODY,{"derivedFrom":makeQuery(id+"F5.opPattern","COPY",BODY,{"derivedFrom":makeQuery(id+"F1.opExtrude","SWEPT_BODY",BODY,{"disambiguationData":[OSD([sQuery(id+"F0.wireOp",EDGE,"E0.rect.bottom"),sQuery(id+"F0.wireOp",EDGE,"E0.rect.top"),sQuery(id+"F0.wireOp",EDGE,"E0.rect.left"),sQuery(id+"F0.wireOp",EDGE,"E0.rect.right"),sQuery(id+"F0.wireOp",EDGE,"E1.rect.bottom"),sQuery(id+"F0.wireOp",EDGE,"E1.rect.top"),sQuery(id+"F0.wireOp",EDGE,"E1.rect.left"),sQuery(id+"F0.wireOp",EDGE,"E1.rect.right")])]}),"instanceName":"1"}),"instanceName":"1"}),"instanceName":"1"});
            var Q4;
            Q4=qCreatedBy(makeId("Right.planeOp"),FACE);
            transform(context, id + "F14", {"entities" : qUnion([Q0, Q1, Q2, Q3]), "transformType" : TransformType.TRANSLATION_DISTANCE, "transformDirection" : qUnion([Q4]), "distance" : 35 * mm, "makeCopy" : true});
        }
    });
